annotation { "Feature Type Name" : "Feature", "Feature Type Description" : "" }
export const myFeature = defineFeature(function(context is Context, id is Id, definition is map)
    precondition{}
    {
        {
            var Q0;
            Q0=qCreatedBy(makeId("Front.planeOp"),FACE);
            var sketch = newSketch(context, id + "F0", { "sketchPlane" : qUnion([Q0])});
            skText(sketch, "E0", { "text": "Nicholas Kim", "fontName": "OpenSans-Regular.ttf"});
            const initialGuessF0  = {"E0": [-0.22058, -0.01557, 1, 0, 0.05267]};
            skSetInitialGuess(sketch, initialGuessF0);
            skSolve(sketch);
        }
        {
            var Q0;
            Q0=qCreatedBy(makeId("Front.planeOp"),FACE);
            var sketch = newSketch(context, id + "F1", { "sketchPlane" : qUnion([Q0])});
            skLineSegment(sketch, "E1", {"start": v(-220.5, 40.22) * mm, "end": v(-220.5, 52.92) * mm, "construction": true});
            skLineSegment(sketch, "E2", {"start": v(-220.5, 40.22) * mm, "end": v(-233.2, 40.22) * mm, "construction": true});
            skLineSegment(sketch, "E3", {"start": v(220.38, -15.51) * mm, "end": v(220.38, -28.21) * mm, "construction": true});
            skLineSegment(sketch, "E4", {"start": v(220.38, -15.51) * mm, "end": v(233.08, -15.51) * mm, "construction": true});
            skLineSegment(sketch, "E5", {"start": v(-220.5, 52.92) * mm, "end": v(-226.85, 52.92) * mm});
            skLineSegment(sketch, "E6", {"start": v(-233.2, 46.57) * mm, "end": v(-233.2, 40.22) * mm});
            skLineSegment(sketch, "E7", {"start": v(233.08, -15.51) * mm, "end": v(233.08, -21.86) * mm});
            skLineSegment(sketch, "E8", {"start": v(220.38, -28.21) * mm, "end": v(226.73, -28.21) * mm});
            skLineSegment(sketch, "E9", {"start": v(-233.2, 40.22) * mm, "end": v(-233.2, -21.86) * mm});
            skLineSegment(sketch, "E10", {"start": v(-226.85, -28.21) * mm, "end": v(220.38, -28.21) * mm});
            skLineSegment(sketch, "E11", {"start": v(233.08, -15.51) * mm, "end": v(233.08, 46.57) * mm});
            skLineSegment(sketch, "E12", {"start": v(226.73, 52.92) * mm, "end": v(-220.5, 52.92) * mm});
            skLineSegment(sketch, "E13", {"start": v(-220.5, 33.87) * mm, "end": v(-220.5, -11.48) * mm});
            skLineSegment(sketch, "E14", {"start": v(-214.12, -17.83) * mm, "end": v(214.07, -15.55) * mm});
            skLineSegment(sketch, "E15", {"start": v(214.03, 40.22) * mm, "end": v(-214.15, 40.22) * mm});
            skLineSegment(sketch, "E16", {"start": v(220.38, 33.87) * mm, "end": v(220.38, -9.2) * mm});
            skPoint(sketch, "E17.visualSharp", {"position": v(-233.2, 52.92) * mm});
            skArc(sketch, "E17.filletArc", {"start": v(-226.85, 52.92) * mm, "mid": v(-231.34, 51.06) * mm, "end": v(-233.2, 46.57) * mm});
            skPoint(sketch, "E18.visualSharp", {"position": v(-233.2, -28.21) * mm});
            skArc(sketch, "E18.filletArc", {"start": v(-233.2, -21.86) * mm, "mid": v(-231.34, -26.35) * mm, "end": v(-226.85, -28.21) * mm});
            skPoint(sketch, "E19.visualSharp", {"position": v(233.08, -28.21) * mm});
            skArc(sketch, "E19.filletArc", {"start": v(226.73, -28.21) * mm, "mid": v(231.22, -26.35) * mm, "end": v(233.08, -21.86) * mm});
            skPoint(sketch, "E20.visualSharp", {"position": v(233.08, 52.92) * mm});
            skArc(sketch, "E20.filletArc", {"start": v(233.08, 46.57) * mm, "mid": v(231.22, 51.06) * mm, "end": v(226.73, 52.92) * mm});
            skPoint(sketch, "E21.visualSharp", {"position": v(-220.5, 40.22) * mm});
            skArc(sketch, "E21.filletArc", {"start": v(-214.15, 40.22) * mm, "mid": v(-218.64, 38.36) * mm, "end": v(-220.5, 33.87) * mm});
            skPoint(sketch, "E22.visualSharp", {"position": v(220.38, 40.22) * mm});
            skArc(sketch, "E22.filletArc", {"start": v(220.38, 33.87) * mm, "mid": v(218.52, 38.36) * mm, "end": v(214.03, 40.22) * mm});
            skPoint(sketch, "E23.visualSharp", {"position": v(220.38, -15.51) * mm});
            skArc(sketch, "E23.filletArc", {"start": v(214.07, -15.55) * mm, "mid": v(218.54, -13.68) * mm, "end": v(220.38, -9.2) * mm});
            skPoint(sketch, "E24.visualSharp", {"position": v(-220.5, -17.86) * mm});
            skArc(sketch, "E24.filletArc", {"start": v(-220.5, -11.48) * mm, "mid": v(-218.63, -15.98) * mm, "end": v(-214.12, -17.83) * mm});
            skSolve(sketch);
        }
        {
            var Q0;
            Q0 = qSketchRegion(id + "F0", true);
            extrude(context, id + "F2", {"entities" : qUnion([Q0]), "depth" : 25.4 * mm, "offsetDistance" : 25.4 * mm});
        }
        {
            var Q0;
            Q0=qCreatedBy(makeId("Front.planeOp"),FACE);
            var sketch = newSketch(context, id + "F3", { "sketchPlane" : qUnion([Q0])});
            skLineSegment(sketch, "E25.bottom", {"start": v(226.54, -28.17) * mm, "end": v(-227.05, -28.17) * mm});
            skLineSegment(sketch, "E25.top", {"start": v(226.54, 53.04) * mm, "end": v(-227.05, 53.04) * mm});
            skLineSegment(sketch, "E25.left", {"start": v(232.89, -21.82) * mm, "end": v(232.89, 46.7) * mm});
            skLineSegment(sketch, "E25.right", {"start": v(-233.4, -21.82) * mm, "end": v(-233.4, 46.7) * mm});
            skPoint(sketch, "E26.visualSharp", {"position": v(-233.4, 53.04) * mm});
            skArc(sketch, "E26.filletArc", {"start": v(-227.05, 53.04) * mm, "mid": v(-231.54, 51.18) * mm, "end": v(-233.4, 46.7) * mm});
            skPoint(sketch, "E27.visualSharp", {"position": v(-233.4, -28.17) * mm});
            skArc(sketch, "E27.filletArc", {"start": v(-233.4, -21.82) * mm, "mid": v(-231.54, -26.31) * mm, "end": v(-227.05, -28.17) * mm});
            skPoint(sketch, "E28.visualSharp", {"position": v(232.89, -28.17) * mm});
            skArc(sketch, "E28.filletArc", {"start": v(226.54, -28.17) * mm, "mid": v(231.03, -26.31) * mm, "end": v(232.89, -21.82) * mm});
            skPoint(sketch, "E29.visualSharp", {"position": v(232.89, 53.04) * mm});
            skArc(sketch, "E29.filletArc", {"start": v(232.89, 46.7) * mm, "mid": v(231.03, 51.18) * mm, "end": v(226.54, 53.04) * mm});
            skSolve(sketch);
        }
        {
            var Q0;
            Q0 = qSketchRegion(id + "F3", true);
            extrude(context, id + "F4", {"entities" : qUnion([Q0]), "operationType" : NewBodyOperationType.ADD, "depth" : 10.16 * mm, "offsetDistance" : 25.4 * mm});
        }
        {
            var Q0;
            Q0=makeQuery(id+"F1.imprint","IMPRINT",FACE,{"disambiguationData":[TD([[makeQuery(id+"F1.imprint","IMPRINT",EDGE,{"derivedFrom":sQuery(id+"F1.wireOp",EDGE,"E5")}),1.0]])]});
            extrude(context, id + "F5", {"entities" : qUnion([Q0]), "depth" : 25.4 * mm, "offsetDistance" : 25.4 * mm});
        }
    });